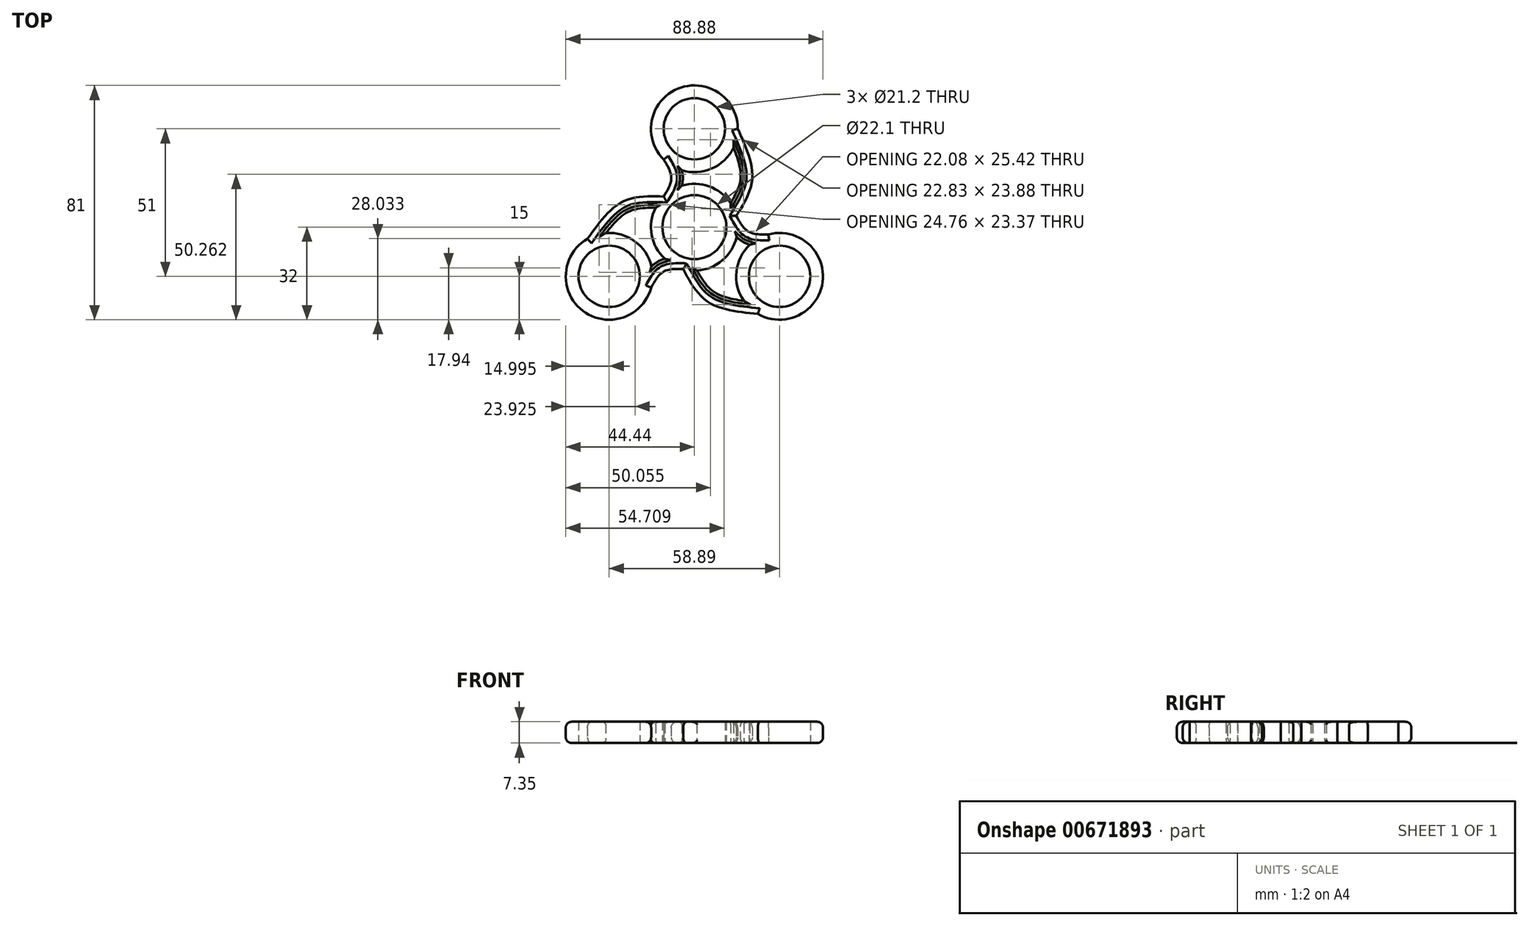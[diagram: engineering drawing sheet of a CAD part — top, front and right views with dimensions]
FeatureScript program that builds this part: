
annotation { "Feature Type Name" : "Feature", "Feature Type Description" : "" }
export const myFeature = defineFeature(function(context is Context, id is Id, definition is map)
    precondition{}
    {
        {
            var Q0;
            Q0=qCreatedBy(makeId("Top.planeOp"),FACE);
            var sketch = newSketch(context, id + "F0", { "sketchPlane" : qUnion([Q0])});
            skCircle(sketch, "E0", {"center": v(0, 0) * mm, "radius": 11.05 * mm});
            skCircle(sketch, "E1", {"center": v(0, 0) * mm, "radius": 15 * mm});
            skLineSegment(sketch, "E2", {"start": v(0, 0) * mm, "end": v(29.44, -17) * mm, "construction": true});
            skLineSegment(sketch, "E3", {"start": v(0, 0) * mm, "end": v(-29.44, -17) * mm, "construction": true});
            skLineSegment(sketch, "E4", {"start": v(0, 0) * mm, "end": v(0, 34) * mm, "construction": true});
            skCircle(sketch, "E5", {"center": v(-29.44, -17) * mm, "radius": 10.6 * mm});
            skCircle(sketch, "E6", {"center": v(29.44, -17) * mm, "radius": 10.6 * mm});
            skCircle(sketch, "E7", {"center": v(0, 34) * mm, "radius": 10.6 * mm});
            skCircle(sketch, "E8", {"center": v(0, 34) * mm, "radius": 15 * mm});
            skCircle(sketch, "E9", {"center": v(29.44, -17) * mm, "radius": 15 * mm});
            skCircle(sketch, "E10", {"center": v(-29.44, -17) * mm, "radius": 15 * mm});
            skLineSegment(sketch, "E11", {"start": v(-29.44, -17) * mm, "end": v(-45.5, 10.82) * mm, "construction": true});
            skLineSegment(sketch, "E12", {"start": v(0, 0) * mm, "end": v(-20.49, 0) * mm, "construction": true});
            skLineSegment(sketch, "E13", {"start": v(-20.49, 0) * mm, "end": v(31.92, 0) * mm, "construction": true});
            skLineSegment(sketch, "E14", {"start": v(0, 0) * mm, "end": v(-29.1, 29.1) * mm, "construction": true});
            skLineSegment(sketch, "E15", {"start": v(-14.72, -8.5) * mm, "end": v(-24.72, 8.82) * mm, "construction": true});
            skFitSpline(sketch, "E16", {"points": [v(-36.94, -4) * mm, v(-24.72, 8.82) * mm, v(-10.6, 10.6) * mm], "startDerivative": vector(21.4, 29.75) * mm, "endDerivative": vector(31.45, -1.08) * mm});
            skFitSpline(sketch, "E17.0", {"points": [v(-33.7, -6.35) * mm, v(-32.8, -5.1) * mm, v(-31.05, -2.67) * mm, v(-28.9, 0.06) * mm, v(-27.18, 1.94) * mm, v(-25.91, 3.17) * mm, v(-24.66, 4.2) * mm, v(-23.74, 4.8) * mm, v(-23.14, 5.14) * mm, v(-22.75, 5.34) * mm, v(-22.04, 5.66) * mm, v(-20.95, 6.04) * mm, v(-19.53, 6.36) * mm, v(-17.98, 6.57) * mm, v(-16.32, 6.68) * mm, v(-13.96, 6.72) * mm, v(-12.05, 6.65) * mm, v(-10.74, 6.6) * mm]});
            skLineSegment(sketch, "E18", {"start": v(-36.94, -4) * mm, "end": v(-33.7, -6.35) * mm});
            skLineSegment(sketch, "E19", {"start": v(-10.74, 6.6) * mm, "end": v(-10.6, 10.6) * mm});
            skLineSegment(sketch, "E20", {"start": v(-29.44, -17) * mm, "end": v(-5.89, -23.31) * mm, "construction": true});
            skLineSegment(sketch, "E21", {"start": v(0, 0) * mm, "end": v(-4.76, -17.75) * mm, "construction": true});
            skLineSegment(sketch, "E22", {"start": v(-14.72, -8.5) * mm, "end": v(-10.72, -15.43) * mm, "construction": true});
            skFitSpline(sketch, "E23", {"points": [v(-14.96, -20.88) * mm, v(-10.72, -15.43) * mm, v(-3.88, -14.49) * mm], "startDerivative": vector(7.16, 13.17) * mm, "endDerivative": vector(14.98, -0.38) * mm});
            skFitSpline(sketch, "E24.0", {"points": [v(-18.47, -18.97) * mm, v(-18.17, -18.42) * mm, v(-17.7, -17.55) * mm, v(-16.97, -16.34) * mm, v(-16.36, -15.42) * mm, v(-15.66, -14.5) * mm, v(-14.98, -13.74) * mm, v(-14.37, -13.15) * mm, v(-13.86, -12.73) * mm, v(-13.32, -12.33) * mm, v(-12.73, -11.96) * mm, v(-12.1, -11.63) * mm, v(-11.49, -11.36) * mm, v(-10.87, -11.13) * mm, v(-10.06, -10.9) * mm, v(-9.06, -10.68) * mm, v(-7.91, -10.54) * mm, v(-6.8, -10.47) * mm, v(-5.4, -10.45) * mm, v(-4.4, -10.47) * mm, v(-3.78, -10.5) * mm]});
            skLineSegment(sketch, "E25", {"start": v(-3.78, -10.5) * mm, "end": v(-3.88, -14.49) * mm});
            skLineSegment(sketch, "E26", {"start": v(-18.47, -18.97) * mm, "end": v(-14.96, -20.88) * mm});
            skLineSegment(sketch, "E27", {"start": v(14.72, -8.5) * mm, "end": v(4.72, -25.82) * mm, "construction": true});
            skLineSegment(sketch, "E28", {"start": v(29.44, -17) * mm, "end": v(17.37, -37.92) * mm, "construction": true});
            skLineSegment(sketch, "E29", {"start": v(0, 0) * mm, "end": v(0, -36.28) * mm, "construction": true});
            skLineSegment(sketch, "E30", {"start": v(0, 0) * mm, "end": v(-12.58, -46.95) * mm, "construction": true});
            skFitSpline(sketch, "E31", {"points": [v(21.94, -30) * mm, v(4.72, -25.82) * mm, v(-3.88, -14.49) * mm], "startDerivative": vector(-36.46, 3.67) * mm, "endDerivative": vector(-14.8, 27.77) * mm});
            skFitSpline(sketch, "E32.0", {"points": [v(22.35, -26.01) * mm, v(20.83, -25.86) * mm, v(17.84, -25.56) * mm, v(14.4, -25.05) * mm, v(11.91, -24.51) * mm, v(10.21, -24.03) * mm, v(8.7, -23.45) * mm, v(7.72, -22.96) * mm, v(7.12, -22.61) * mm, v(6.75, -22.37) * mm, v(6.11, -21.92) * mm, v(5.25, -21.16) * mm, v(4.26, -20.1) * mm, v(3.3, -18.86) * mm, v(2.37, -17.47) * mm, v(1.16, -15.45) * mm, v(0.26, -13.77) * mm, v(-0.35, -12.6) * mm]});
            skLineSegment(sketch, "E33", {"start": v(-3.88, -14.49) * mm, "end": v(-0.35, -12.6) * mm});
            skLineSegment(sketch, "E34", {"start": v(21.94, -30) * mm, "end": v(22.35, -26.01) * mm});
            skLineSegment(sketch, "E35", {"start": v(14.72, -8.5) * mm, "end": v(18.72, -1.57) * mm, "construction": true});
            skLineSegment(sketch, "E36", {"start": v(29.44, -17) * mm, "end": v(22.14, 10.24) * mm, "construction": true});
            skLineSegment(sketch, "E37", {"start": v(0, 0) * mm, "end": v(38.21, 10.24) * mm, "construction": true});
            skFitSpline(sketch, "E38", {"points": [v(25.56, -2.51) * mm, v(18.72, -1.57) * mm, v(14.49, 3.88) * mm], "startDerivative": vector(-14.98, -0.38) * mm, "endDerivative": vector(-7.16, 13.17) * mm});
            skFitSpline(sketch, "E39.0", {"points": [v(25.66, -6.5) * mm, v(25.04, -6.53) * mm, v(24.05, -6.55) * mm, v(22.64, -6.53) * mm, v(21.53, -6.46) * mm, v(20.38, -6.32) * mm, v(19.39, -6.1) * mm, v(18.57, -5.87) * mm, v(17.96, -5.64) * mm, v(17.34, -5.37) * mm, v(16.72, -5.04) * mm, v(16.13, -4.67) * mm, v(15.58, -4.27) * mm, v(15.08, -3.85) * mm, v(14.46, -3.26) * mm, v(13.78, -2.5) * mm, v(13.08, -1.58) * mm, v(12.47, -0.66) * mm, v(11.75, 0.55) * mm, v(11.27, 1.42) * mm, v(10.98, 1.97) * mm]});
            skLineSegment(sketch, "E40", {"start": v(10.98, 1.97) * mm, "end": v(14.49, 3.88) * mm});
            skLineSegment(sketch, "E41", {"start": v(25.66, -6.5) * mm, "end": v(25.56, -2.51) * mm});
            skLineSegment(sketch, "E42", {"start": v(0, 17) * mm, "end": v(20, 17) * mm, "construction": true});
            skLineSegment(sketch, "E43", {"start": v(0, 34) * mm, "end": v(39.07, 34) * mm, "construction": true});
            skFitSpline(sketch, "E44", {"points": [v(14.49, 3.88) * mm, v(20, 17) * mm, v(15, 34) * mm], "startDerivative": vector(16.66, 26.7) * mm, "endDerivative": vector(-15.06, 33.41) * mm});
            skFitSpline(sketch, "E45.0", {"points": [v(11.1, 6) * mm, v(11.79, 7.11) * mm, v(12.8, 8.73) * mm, v(13.94, 10.79) * mm, v(14.68, 12.29) * mm, v(15.27, 13.73) * mm, v(15.7, 15.13) * mm, v(15.92, 16.25) * mm, v(16, 17.03) * mm, v(16.02, 17.48) * mm, v(16.03, 18.16) * mm, v(15.96, 19.26) * mm, v(15.7, 20.86) * mm, v(15.27, 22.57) * mm, v(14.5, 25) * mm, v(13.21, 28.23) * mm, v(11.98, 30.96) * mm, v(11.35, 32.36) * mm]});
            skLineSegment(sketch, "E46", {"start": v(11.35, 32.36) * mm, "end": v(15, 34) * mm});
            skLineSegment(sketch, "E47", {"start": v(11.1, 6) * mm, "end": v(14.49, 3.88) * mm});
            skLineSegment(sketch, "E48", {"start": v(0, 17) * mm, "end": v(-8, 17) * mm, "construction": true});
            skLineSegment(sketch, "E49", {"start": v(0, 34) * mm, "end": v(-17.53, 16.47) * mm, "construction": true});
            skFitSpline(sketch, "E50", {"points": [v(-10.6, 23.4) * mm, v(-8, 17) * mm, v(-10.6, 10.6) * mm], "startDerivative": vector(7.82, -12.79) * mm, "endDerivative": vector(-7.82, -12.79) * mm});
            skFitSpline(sketch, "E51.0", {"points": [v(-7.2, 25.48) * mm, v(-6.87, 24.95) * mm, v(-6.35, 24.1) * mm, v(-5.66, 22.87) * mm, v(-5.17, 21.88) * mm, v(-4.72, 20.8) * mm, v(-4.4, 19.84) * mm, v(-4.2, 19.02) * mm, v(-4.1, 18.37) * mm, v(-4.02, 17.7) * mm, v(-4, 17) * mm, v(-4.02, 16.3) * mm, v(-4.1, 15.63) * mm, v(-4.2, 14.98) * mm, v(-4.4, 14.16) * mm, v(-4.72, 13.2) * mm, v(-5.17, 12.12) * mm, v(-5.66, 11.13) * mm, v(-6.35, 9.9) * mm, v(-6.87, 9.05) * mm, v(-7.2, 8.52) * mm]});
            skLineSegment(sketch, "E52", {"start": v(-10.6, 10.6) * mm, "end": v(-7.2, 8.52) * mm});
            skLineSegment(sketch, "E53", {"start": v(-10.6, 23.4) * mm, "end": v(-7.2, 25.48) * mm});
            skSolve(sketch);
        }
        {
            var Q0;
            {var subQ0=sQuery(id+"F0.wireOp",EDGE,"E25");Q0=makeQuery(id+"F0.imprint","IMPRINT",FACE,{"disambiguationData":[TD([[makeQuery(id+"F0.imprint","IMPRINT",EDGE,{"derivedFrom":subQ0}),-1.0]])]});}
            var Q1;
            Q1=makeQuery(id+"F0.imprint","IMPRINT",FACE,{"disambiguationData":[TD([[makeQuery(id+"F0.imprint","IMPRINT",EDGE,{"derivedFrom":sQuery(id+"F0.wireOp",EDGE,"E0")}),-1.0]])]});
            var Q2;
            {var subQ0=sQuery(id+"F0.wireOp",EDGE,"E23");Q2=makeQuery(id+"F0.imprint","IMPRINT",FACE,{"disambiguationData":[TD([[makeQuery(id+"F0.imprint","IMPRINT",EDGE,{"derivedFrom":subQ0}),1.0]])]});}
            var Q3;
            {var subQ0=sQuery(id+"F0.wireOp",EDGE,"E26");Q3=makeQuery(id+"F0.imprint","IMPRINT",FACE,{"disambiguationData":[TD([[makeQuery(id+"F0.imprint","IMPRINT",EDGE,{"derivedFrom":subQ0}),1.0]])]});}
            var Q4;
            Q4=makeQuery(id+"F0.imprint","IMPRINT",FACE,{"disambiguationData":[TD([[makeQuery(id+"F0.imprint","IMPRINT",EDGE,{"derivedFrom":sQuery(id+"F0.wireOp",EDGE,"E5")}),-1.0]])]});
            var Q5;
            {var subQ0=sQuery(id+"F0.wireOp",EDGE,"E18");Q5=makeQuery(id+"F0.imprint","IMPRINT",FACE,{"disambiguationData":[TD([[makeQuery(id+"F0.imprint","IMPRINT",EDGE,{"derivedFrom":subQ0}),1.0]])]});}
            var Q6;
            {var subQ0=sQuery(id+"F0.wireOp",EDGE,"E16");Q6=makeQuery(id+"F0.imprint","IMPRINT",FACE,{"disambiguationData":[TD([[makeQuery(id+"F0.imprint","IMPRINT",EDGE,{"derivedFrom":subQ0}),-1.0]])]});}
            var Q7;
            {var subQ0=sQuery(id+"F0.wireOp",EDGE,"E19");Q7=makeQuery(id+"F0.imprint","IMPRINT",FACE,{"disambiguationData":[TD([[makeQuery(id+"F0.imprint","IMPRINT",EDGE,{"derivedFrom":subQ0}),1.0]])]});}
            var Q8;
            {var subQ0=sQuery(id+"F0.wireOp",EDGE,"E52");Q8=makeQuery(id+"F0.imprint","IMPRINT",FACE,{"disambiguationData":[TD([[makeQuery(id+"F0.imprint","IMPRINT",EDGE,{"derivedFrom":subQ0}),1.0]])]});}
            var Q9;
            {var subQ0=sQuery(id+"F0.wireOp",EDGE,"E50");Q9=makeQuery(id+"F0.imprint","IMPRINT",FACE,{"disambiguationData":[TD([[makeQuery(id+"F0.imprint","IMPRINT",EDGE,{"derivedFrom":subQ0}),1.0]])]});}
            var Q10;
            Q10=makeQuery(id+"F0.imprint","IMPRINT",FACE,{"disambiguationData":[TD([[makeQuery(id+"F0.imprint","IMPRINT",EDGE,{"derivedFrom":sQuery(id+"F0.wireOp",EDGE,"E7")}),-1.0]])]});
            var Q11;
            {var subQ0=sQuery(id+"F0.wireOp",EDGE,"E53");Q11=makeQuery(id+"F0.imprint","IMPRINT",FACE,{"disambiguationData":[TD([[makeQuery(id+"F0.imprint","IMPRINT",EDGE,{"derivedFrom":subQ0}),-1.0]])]});}
            var Q12;
            {var subQ0=sQuery(id+"F0.wireOp",EDGE,"E46");Q12=makeQuery(id+"F0.imprint","IMPRINT",FACE,{"disambiguationData":[TD([[makeQuery(id+"F0.imprint","IMPRINT",EDGE,{"derivedFrom":subQ0}),-1.0]])]});}
            var Q13;
            {var subQ0=sQuery(id+"F0.wireOp",EDGE,"E44");Q13=makeQuery(id+"F0.imprint","IMPRINT",FACE,{"disambiguationData":[TD([[makeQuery(id+"F0.imprint","IMPRINT",EDGE,{"derivedFrom":subQ0}),1.0]])]});}
            var Q14;
            {var subQ0=sQuery(id+"F0.wireOp",EDGE,"E47");Q14=makeQuery(id+"F0.imprint","IMPRINT",FACE,{"disambiguationData":[TD([[makeQuery(id+"F0.imprint","IMPRINT",EDGE,{"derivedFrom":subQ0}),1.0]])]});}
            var Q15;
            {var subQ0=sQuery(id+"F0.wireOp",EDGE,"E40");Q15=makeQuery(id+"F0.imprint","IMPRINT",FACE,{"disambiguationData":[TD([[makeQuery(id+"F0.imprint","IMPRINT",EDGE,{"derivedFrom":subQ0}),-1.0]])]});}
            var Q16;
            {var subQ0=sQuery(id+"F0.wireOp",EDGE,"E38");Q16=makeQuery(id+"F0.imprint","IMPRINT",FACE,{"disambiguationData":[TD([[makeQuery(id+"F0.imprint","IMPRINT",EDGE,{"derivedFrom":subQ0}),1.0]])]});}
            var Q17;
            {var subQ0=sQuery(id+"F0.wireOp",EDGE,"E41");Q17=makeQuery(id+"F0.imprint","IMPRINT",FACE,{"disambiguationData":[TD([[makeQuery(id+"F0.imprint","IMPRINT",EDGE,{"derivedFrom":subQ0}),1.0]])]});}
            var Q18;
            Q18=makeQuery(id+"F0.imprint","IMPRINT",FACE,{"disambiguationData":[TD([[makeQuery(id+"F0.imprint","IMPRINT",EDGE,{"derivedFrom":sQuery(id+"F0.wireOp",EDGE,"E6")}),-1.0]])]});
            var Q19;
            {var subQ0=sQuery(id+"F0.wireOp",EDGE,"E34");Q19=makeQuery(id+"F0.imprint","IMPRINT",FACE,{"disambiguationData":[TD([[makeQuery(id+"F0.imprint","IMPRINT",EDGE,{"derivedFrom":subQ0}),1.0]])]});}
            var Q20;
            {var subQ0=sQuery(id+"F0.wireOp",EDGE,"E31");Q20=makeQuery(id+"F0.imprint","IMPRINT",FACE,{"disambiguationData":[TD([[makeQuery(id+"F0.imprint","IMPRINT",EDGE,{"derivedFrom":subQ0}),-1.0]])]});}
            var Q21;
            {var subQ0=sQuery(id+"F0.wireOp",EDGE,"E33");Q21=makeQuery(id+"F0.imprint","IMPRINT",FACE,{"disambiguationData":[TD([[makeQuery(id+"F0.imprint","IMPRINT",EDGE,{"derivedFrom":subQ0}),-1.0]])]});}
            extrude(context, id + "F1", {"entities" : qUnion([Q0, Q1, Q2, Q3, Q4, Q5, Q6, Q7, Q8, Q9, Q10, Q11, Q12, Q13, Q14, Q15, Q16, Q17, Q18, Q19, Q20, Q21]), "depth" : 7.35 * mm, "offsetDistance" : 25 * mm});
        }
        {
            var Q0;
            {var subQ0=sQuery(id+"F0.wireOp",EDGE,"E10");Q0=makeQuery(id+"F1.opExtrude","CAP_EDGE",EDGE,{"disambiguationData":[OSD([subQ0]),TDD([makeQuery(id+"F0.imprint","IMPRINT",EDGE,{"disambiguationData":[TD([[makeQuery(id+"F0.imprint","INTERSECT",VERTEX,{"derivedFrom":[subQ0,sQuery(id+"F0.wireOp",EDGE,"E16"),sQuery(id+"F0.wireOp",EDGE,"E18")]}),-1.0]])],"derivedFrom":subQ0})])],"isStart":false});}
            var Q1;
            Q1=makeQuery(id+"F1.opExtrude","CAP_EDGE",EDGE,{"disambiguationData":[OSD([sQuery(id+"F0.wireOp",EDGE,"E23")])],"isStart":false});
            var Q2;
            Q2=makeQuery(id+"F1.opExtrude","CAP_EDGE",EDGE,{"disambiguationData":[OSD([sQuery(id+"F0.wireOp",EDGE,"E31")])],"isStart":false});
            var Q3;
            {var subQ0=sQuery(id+"F0.wireOp",EDGE,"E9");Q3=makeQuery(id+"F1.opExtrude","CAP_EDGE",EDGE,{"disambiguationData":[OSD([subQ0]),TDD([makeQuery(id+"F0.imprint","IMPRINT",EDGE,{"disambiguationData":[TD([[makeQuery(id+"F0.imprint","INTERSECT",VERTEX,{"derivedFrom":[subQ0,sQuery(id+"F0.wireOp",EDGE,"E31"),sQuery(id+"F0.wireOp",EDGE,"E34")]}),-1.0]])],"derivedFrom":subQ0})])],"isStart":false});}
            var Q4;
            Q4=makeQuery(id+"F1.opExtrude","CAP_EDGE",EDGE,{"disambiguationData":[OSD([sQuery(id+"F0.wireOp",EDGE,"E38")])],"isStart":false});
            var Q5;
            Q5=makeQuery(id+"F1.opExtrude","CAP_EDGE",EDGE,{"disambiguationData":[OSD([sQuery(id+"F0.wireOp",EDGE,"E44")])],"isStart":false});
            var Q6;
            {var subQ0=sQuery(id+"F0.wireOp",EDGE,"E8");Q6=makeQuery(id+"F1.opExtrude","CAP_EDGE",EDGE,{"disambiguationData":[OSD([subQ0]),TDD([makeQuery(id+"F0.imprint","IMPRINT",EDGE,{"disambiguationData":[TD([[makeQuery(id+"F0.imprint","INTERSECT",VERTEX,{"derivedFrom":[subQ0,sQuery(id+"F0.wireOp",EDGE,"E44"),sQuery(id+"F0.wireOp",EDGE,"E46")]}),-1.0]])],"derivedFrom":subQ0})])],"isStart":false});}
            var Q7;
            Q7=makeQuery(id+"F1.opExtrude","CAP_EDGE",EDGE,{"disambiguationData":[OSD([sQuery(id+"F0.wireOp",EDGE,"E50")])],"isStart":false});
            var Q8;
            Q8=makeQuery(id+"F1.opExtrude","CAP_EDGE",EDGE,{"disambiguationData":[OSD([sQuery(id+"F0.wireOp",EDGE,"E16")])],"isStart":false});
            var Q9;
            {var subQ0=sQuery(id+"F0.wireOp",EDGE,"E10");Q9=makeQuery(id+"F1.opExtrude","CAP_EDGE",EDGE,{"disambiguationData":[OSD([subQ0]),TDD([makeQuery(id+"F0.imprint","IMPRINT",EDGE,{"disambiguationData":[TD([[makeQuery(id+"F0.imprint","INTERSECT",VERTEX,{"derivedFrom":[subQ0,sQuery(id+"F0.wireOp",EDGE,"E16"),sQuery(id+"F0.wireOp",EDGE,"E18")]}),-1.0]])],"derivedFrom":subQ0})])],"isStart":true});}
            var Q10;
            Q10=makeQuery(id+"F1.opExtrude","CAP_EDGE",EDGE,{"disambiguationData":[OSD([sQuery(id+"F0.wireOp",EDGE,"E16")])],"isStart":true});
            var Q11;
            Q11=makeQuery(id+"F1.opExtrude","CAP_EDGE",EDGE,{"disambiguationData":[OSD([sQuery(id+"F0.wireOp",EDGE,"E50")])],"isStart":true});
            var Q12;
            {var subQ0=sQuery(id+"F0.wireOp",EDGE,"E8");Q12=makeQuery(id+"F1.opExtrude","CAP_EDGE",EDGE,{"disambiguationData":[OSD([subQ0]),TDD([makeQuery(id+"F0.imprint","IMPRINT",EDGE,{"disambiguationData":[TD([[makeQuery(id+"F0.imprint","INTERSECT",VERTEX,{"derivedFrom":[subQ0,sQuery(id+"F0.wireOp",EDGE,"E44"),sQuery(id+"F0.wireOp",EDGE,"E46")]}),-1.0]])],"derivedFrom":subQ0})])],"isStart":true});}
            var Q13;
            Q13=makeQuery(id+"F1.opExtrude","CAP_EDGE",EDGE,{"disambiguationData":[OSD([sQuery(id+"F0.wireOp",EDGE,"E44")])],"isStart":true});
            var Q14;
            Q14=makeQuery(id+"F1.opExtrude","CAP_EDGE",EDGE,{"disambiguationData":[OSD([sQuery(id+"F0.wireOp",EDGE,"E38")])],"isStart":true});
            var Q15;
            {var subQ0=sQuery(id+"F0.wireOp",EDGE,"E9");Q15=makeQuery(id+"F1.opExtrude","CAP_EDGE",EDGE,{"disambiguationData":[OSD([subQ0]),TDD([makeQuery(id+"F0.imprint","IMPRINT",EDGE,{"disambiguationData":[TD([[makeQuery(id+"F0.imprint","INTERSECT",VERTEX,{"derivedFrom":[subQ0,sQuery(id+"F0.wireOp",EDGE,"E31"),sQuery(id+"F0.wireOp",EDGE,"E34")]}),-1.0]])],"derivedFrom":subQ0})])],"isStart":true});}
            var Q16;
            Q16=makeQuery(id+"F1.opExtrude","CAP_EDGE",EDGE,{"disambiguationData":[OSD([sQuery(id+"F0.wireOp",EDGE,"E31")])],"isStart":true});
            var Q17;
            Q17=makeQuery(id+"F1.opExtrude","CAP_EDGE",EDGE,{"disambiguationData":[OSD([sQuery(id+"F0.wireOp",EDGE,"E23")])],"isStart":true});
            fillet(context, id + "F2", {"entities" : qUnion([Q0, Q1, Q2, Q3, Q4, Q5, Q6, Q7, Q8, Q9, Q10, Q11, Q12, Q13, Q14, Q15, Q16, Q17]), "radius" : 2 * mm, "tangentPropagation" : true, "allowEdgeOverflow" : false});
        }
        {
            var Q0;
            {var subQ0=sQuery(id+"F0.wireOp",EDGE,"E10");Q0=makeQuery(id+"F1.opExtrude","CAP_EDGE",EDGE,{"disambiguationData":[OSD([subQ0]),TDD([makeQuery(id+"F0.imprint","IMPRINT",EDGE,{"disambiguationData":[TD([[makeQuery(id+"F0.imprint","INTERSECT",VERTEX,{"derivedFrom":[subQ0,sQuery(id+"F0.wireOp",EDGE,"E17.0")]}),1.0]])],"derivedFrom":subQ0})])],"isStart":false});}
            var Q1;
            Q1=makeQuery(id+"F1.opExtrude","CAP_EDGE",EDGE,{"disambiguationData":[OSD([sQuery(id+"F0.wireOp",EDGE,"E17.0")])],"isStart":false});
            var Q2;
            {var subQ0=sQuery(id+"F0.wireOp",EDGE,"E1");Q2=makeQuery(id+"F1.opExtrude","CAP_EDGE",EDGE,{"disambiguationData":[OSD([subQ0]),TDD([makeQuery(id+"F0.imprint","IMPRINT",EDGE,{"disambiguationData":[TD([[makeQuery(id+"F0.imprint","INTERSECT",VERTEX,{"derivedFrom":[subQ0,sQuery(id+"F0.wireOp",EDGE,"E17.0")]}),-1.0]])],"derivedFrom":subQ0})])],"isStart":false});}
            var Q3;
            Q3=makeQuery(id+"F1.opExtrude","CAP_EDGE",EDGE,{"disambiguationData":[OSD([sQuery(id+"F0.wireOp",EDGE,"E24.0")])],"isStart":false});
            var Q4;
            Q4=makeQuery(id+"F1.opExtrude","CAP_EDGE",EDGE,{"disambiguationData":[OSD([sQuery(id+"F0.wireOp",EDGE,"E51.0")])],"isStart":false});
            var Q5;
            {var subQ0=sQuery(id+"F0.wireOp",EDGE,"E1");Q5=makeQuery(id+"F1.opExtrude","CAP_EDGE",EDGE,{"disambiguationData":[OSD([subQ0]),TDD([makeQuery(id+"F0.imprint","IMPRINT",EDGE,{"disambiguationData":[TD([[makeQuery(id+"F0.imprint","INTERSECT",VERTEX,{"derivedFrom":[subQ0,sQuery(id+"F0.wireOp",EDGE,"E45.0")]}),-1.0]])],"derivedFrom":subQ0})])],"isStart":false});}
            var Q6;
            {var subQ0=sQuery(id+"F0.wireOp",EDGE,"E8");Q6=makeQuery(id+"F1.opExtrude","CAP_EDGE",EDGE,{"disambiguationData":[OSD([subQ0]),TDD([makeQuery(id+"F0.imprint","IMPRINT",EDGE,{"disambiguationData":[TD([[makeQuery(id+"F0.imprint","INTERSECT",VERTEX,{"derivedFrom":[subQ0,sQuery(id+"F0.wireOp",EDGE,"E51.0")]}),-1.0]])],"derivedFrom":subQ0})])],"isStart":false});}
            var Q7;
            Q7=makeQuery(id+"F1.opExtrude","CAP_EDGE",EDGE,{"disambiguationData":[OSD([sQuery(id+"F0.wireOp",EDGE,"E45.0")])],"isStart":false});
            var Q8;
            {var subQ0=sQuery(id+"F0.wireOp",EDGE,"E1");Q8=makeQuery(id+"F1.opExtrude","CAP_EDGE",EDGE,{"disambiguationData":[OSD([subQ0]),TDD([makeQuery(id+"F0.imprint","IMPRINT",EDGE,{"disambiguationData":[TD([[makeQuery(id+"F0.imprint","INTERSECT",VERTEX,{"derivedFrom":[subQ0,sQuery(id+"F0.wireOp",EDGE,"E32.0")]}),-1.0]])],"derivedFrom":subQ0})])],"isStart":false});}
            var Q9;
            Q9=makeQuery(id+"F1.opExtrude","CAP_EDGE",EDGE,{"disambiguationData":[OSD([sQuery(id+"F0.wireOp",EDGE,"E32.0")])],"isStart":false});
            var Q10;
            {var subQ0=sQuery(id+"F0.wireOp",EDGE,"E9");Q10=makeQuery(id+"F1.opExtrude","CAP_EDGE",EDGE,{"disambiguationData":[OSD([subQ0]),TDD([makeQuery(id+"F0.imprint","IMPRINT",EDGE,{"disambiguationData":[TD([[makeQuery(id+"F0.imprint","INTERSECT",VERTEX,{"derivedFrom":[subQ0,sQuery(id+"F0.wireOp",EDGE,"E39.0")]}),-1.0]])],"derivedFrom":subQ0})])],"isStart":false});}
            var Q11;
            Q11=makeQuery(id+"F1.opExtrude","CAP_EDGE",EDGE,{"disambiguationData":[OSD([sQuery(id+"F0.wireOp",EDGE,"E39.0")])],"isStart":false});
            var Q12;
            Q12=makeQuery(id+"F1.opExtrude","CAP_EDGE",EDGE,{"disambiguationData":[OSD([sQuery(id+"F0.wireOp",EDGE,"E32.0")])],"isStart":true});
            var Q13;
            {var subQ0=sQuery(id+"F0.wireOp",EDGE,"E9");Q13=makeQuery(id+"F1.opExtrude","CAP_EDGE",EDGE,{"disambiguationData":[OSD([subQ0]),TDD([makeQuery(id+"F0.imprint","IMPRINT",EDGE,{"disambiguationData":[TD([[makeQuery(id+"F0.imprint","INTERSECT",VERTEX,{"derivedFrom":[subQ0,sQuery(id+"F0.wireOp",EDGE,"E39.0")]}),-1.0]])],"derivedFrom":subQ0})])],"isStart":true});}
            var Q14;
            Q14=makeQuery(id+"F1.opExtrude","CAP_EDGE",EDGE,{"disambiguationData":[OSD([sQuery(id+"F0.wireOp",EDGE,"E39.0")])],"isStart":true});
            var Q15;
            {var subQ0=sQuery(id+"F0.wireOp",EDGE,"E1");Q15=makeQuery(id+"F1.opExtrude","CAP_EDGE",EDGE,{"disambiguationData":[OSD([subQ0]),TDD([makeQuery(id+"F0.imprint","IMPRINT",EDGE,{"disambiguationData":[TD([[makeQuery(id+"F0.imprint","INTERSECT",VERTEX,{"derivedFrom":[subQ0,sQuery(id+"F0.wireOp",EDGE,"E32.0")]}),-1.0]])],"derivedFrom":subQ0})])],"isStart":true});}
            var Q16;
            Q16=makeQuery(id+"F1.opExtrude","CAP_EDGE",EDGE,{"disambiguationData":[OSD([sQuery(id+"F0.wireOp",EDGE,"E24.0")])],"isStart":true});
            var Q17;
            {var subQ0=sQuery(id+"F0.wireOp",EDGE,"E1");Q17=makeQuery(id+"F1.opExtrude","CAP_EDGE",EDGE,{"disambiguationData":[OSD([subQ0]),TDD([makeQuery(id+"F0.imprint","IMPRINT",EDGE,{"disambiguationData":[TD([[makeQuery(id+"F0.imprint","INTERSECT",VERTEX,{"derivedFrom":[subQ0,sQuery(id+"F0.wireOp",EDGE,"E17.0")]}),-1.0]])],"derivedFrom":subQ0})])],"isStart":true});}
            var Q18;
            {var subQ0=sQuery(id+"F0.wireOp",EDGE,"E10");Q18=makeQuery(id+"F1.opExtrude","CAP_EDGE",EDGE,{"disambiguationData":[OSD([subQ0]),TDD([makeQuery(id+"F0.imprint","IMPRINT",EDGE,{"disambiguationData":[TD([[makeQuery(id+"F0.imprint","INTERSECT",VERTEX,{"derivedFrom":[subQ0,sQuery(id+"F0.wireOp",EDGE,"E17.0")]}),1.0]])],"derivedFrom":subQ0})])],"isStart":true});}
            var Q19;
            Q19=makeQuery(id+"F1.opExtrude","CAP_EDGE",EDGE,{"disambiguationData":[OSD([sQuery(id+"F0.wireOp",EDGE,"E17.0")])],"isStart":true});
            var Q20;
            Q20=makeQuery(id+"F1.opExtrude","CAP_EDGE",EDGE,{"disambiguationData":[OSD([sQuery(id+"F0.wireOp",EDGE,"E51.0")])],"isStart":true});
            var Q21;
            {var subQ0=sQuery(id+"F0.wireOp",EDGE,"E8");Q21=makeQuery(id+"F1.opExtrude","CAP_EDGE",EDGE,{"disambiguationData":[OSD([subQ0]),TDD([makeQuery(id+"F0.imprint","IMPRINT",EDGE,{"disambiguationData":[TD([[makeQuery(id+"F0.imprint","INTERSECT",VERTEX,{"derivedFrom":[subQ0,sQuery(id+"F0.wireOp",EDGE,"E51.0")]}),-1.0]])],"derivedFrom":subQ0})])],"isStart":true});}
            var Q22;
            {var subQ0=sQuery(id+"F0.wireOp",EDGE,"E1");Q22=makeQuery(id+"F1.opExtrude","CAP_EDGE",EDGE,{"disambiguationData":[OSD([subQ0]),TDD([makeQuery(id+"F0.imprint","IMPRINT",EDGE,{"disambiguationData":[TD([[makeQuery(id+"F0.imprint","INTERSECT",VERTEX,{"derivedFrom":[subQ0,sQuery(id+"F0.wireOp",EDGE,"E45.0")]}),-1.0]])],"derivedFrom":subQ0})])],"isStart":true});}
            var Q23;
            Q23=makeQuery(id+"F1.opExtrude","CAP_EDGE",EDGE,{"disambiguationData":[OSD([sQuery(id+"F0.wireOp",EDGE,"E45.0")])],"isStart":true});
            fillet(context, id + "F3", {"entities" : qUnion([Q0, Q1, Q2, Q3, Q4, Q5, Q6, Q7, Q8, Q9, Q10, Q11, Q12, Q13, Q14, Q15, Q16, Q17, Q18, Q19, Q20, Q21, Q22, Q23]), "radius" : 1 * mm, "tangentPropagation" : true, "allowEdgeOverflow" : false});
        }
    });
